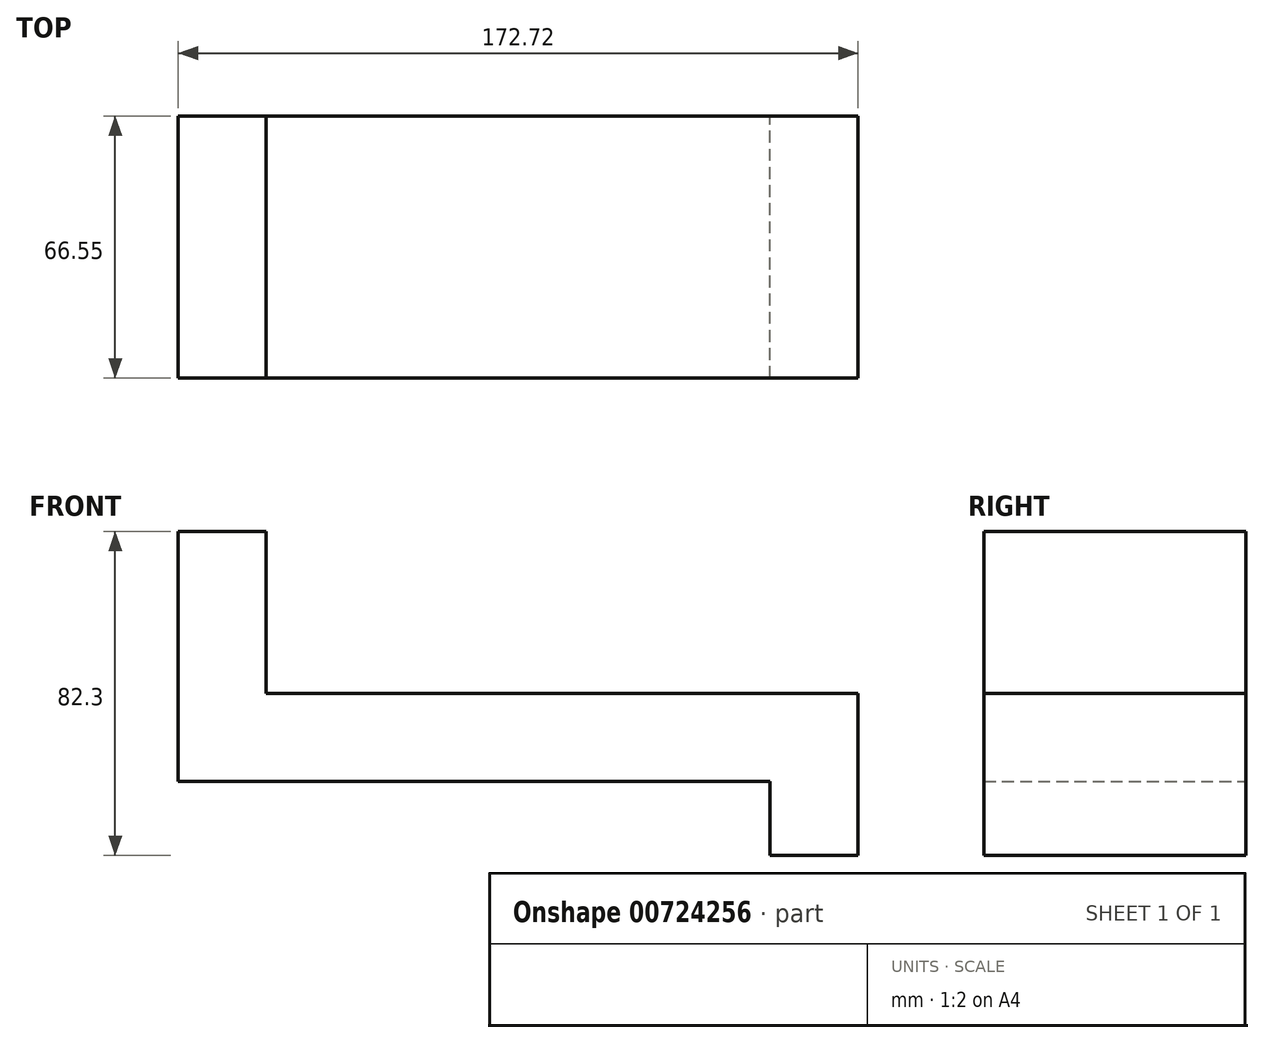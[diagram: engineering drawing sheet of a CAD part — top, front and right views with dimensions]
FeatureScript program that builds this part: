
annotation { "Feature Type Name" : "Feature", "Feature Type Description" : "" }
export const myFeature = defineFeature(function(context is Context, id is Id, definition is map)
    precondition{}
    {
        {
            var Q0;
            Q0=qCreatedBy(makeId("Front.planeOp"),FACE);
            var sketch = newSketch(context, id + "F0", { "sketchPlane" : qUnion([Q0])});
            skLineSegment(sketch, "E0", {"start": v(-65, 68.27) * mm, "end": v(-65, 4.77) * mm});
            skLineSegment(sketch, "E1", {"start": v(-65, 4.77) * mm, "end": v(85.36, 4.77) * mm});
            skLineSegment(sketch, "E2", {"start": v(85.36, 4.77) * mm, "end": v(85.36, -14.03) * mm});
            skLineSegment(sketch, "E3", {"start": v(107.71, -14.03) * mm, "end": v(85.36, -14.03) * mm});
            skLineSegment(sketch, "E4", {"start": v(107.71, -14.03) * mm, "end": v(107.71, 27.12) * mm});
            skLineSegment(sketch, "E5", {"start": v(107.71, 27.12) * mm, "end": v(-42.66, 27.12) * mm});
            skLineSegment(sketch, "E6", {"start": v(-42.66, 27.12) * mm, "end": v(-42.66, 68.27) * mm});
            skLineSegment(sketch, "E7", {"start": v(-42.66, 68.27) * mm, "end": v(-65, 68.27) * mm});
            skSolve(sketch);
        }
        {
            var Q0;
            Q0=makeQuery(id+"F0.imprint","IMPRINT",FACE,{"disambiguationData":[TD([[makeQuery(id+"F0.imprint","IMPRINT",EDGE,{"derivedFrom":sQuery(id+"F0.wireOp",EDGE,"E0")}),1.0]])]});
            extrude(context, id + "F1", {"entities" : qUnion([Q0]), "depth" : 66.55 * mm, "offsetDistance" : 25.4 * mm});
        }
    });
